# Revit family: SH-2122
name_source: partatom
category: Lighting Fixtures
revit_build: Autodesk Revit 2017 (Build: 20160225_1515(x64)
units: mm (PartAtom-declared; Revit-internal decimal feet)

## family parameters
Always vertical = No
Cut with Voids When Loaded = No
Light Source = No
OmniClass Number = 23.80.70.00
OmniClass Title = Lighting
Part Type = Normal
Room Calculation Point = No
Round Connector Dimension = Use Diameter
Shared = Yes
Work Plane-Based = Yes

## types (4) — shared parameters
Body Material = Aluminum
Default Elevation = 121.9 cm
Height = 54.3 cm
IP = IP65
Lamp = E40
Manufacturer = SHOA
Model = SH-2122
URL = https://www.shoaco.com
Voltage/Frequency = 230V/50HZ
Website = www.shoaco.com
Width = 38.0 cm
color rendering index(CRI) = 80<
color temperature = 2000K-5500K
consumption current = 0 A
wattage = 0 W

## per-type parameters (varying)
| type | 2000K | 5500K | Body color |
| Sh-2122(Black color-2000K-E40) | Yes | No | Black color |
| Sh-2122(Black color-5500K-E40) | No | Yes | Black color |
| Sh-2122(White color-2000K-E40) | Yes | No | White color |
| Sh-2122(White color-5500K-E40) | No | Yes | White color |

## geometry (parser evidence)
native form markers: Sweep x11
no freeform markers — native parametric forms only
